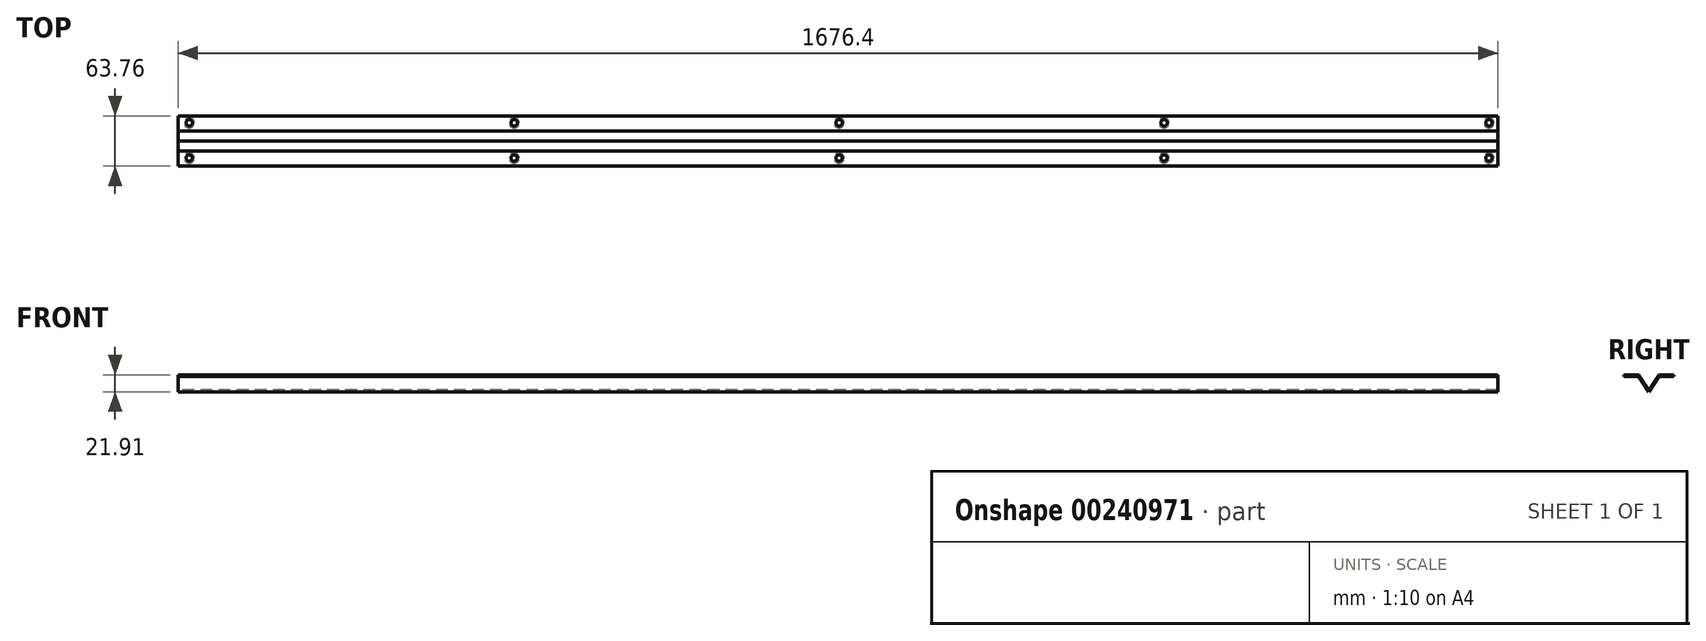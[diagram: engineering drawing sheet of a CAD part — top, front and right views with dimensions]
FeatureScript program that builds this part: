
annotation { "Feature Type Name" : "Feature", "Feature Type Description" : "" }
export const myFeature = defineFeature(function(context is Context, id is Id, definition is map)
    precondition{}
    {
        {
            var Q0;
            Q0=qCreatedBy(makeId("Right.planeOp"),FACE);
            var sketch = newSketch(context, id + "F0", { "sketchPlane" : qUnion([Q0])});
            skLineSegment(sketch, "E0", {"start": v(0, 0) * mm, "end": v(0, 19.61) * mm, "construction": true});
            skLineSegment(sketch, "E1", {"start": v(0, 19.61) * mm, "end": v(80.64, 19.61) * mm, "construction": true});
            skLineSegment(sketch, "E2", {"start": v(0, 19.61) * mm, "end": v(-83.33, 19.61) * mm, "construction": true});
            skLineSegment(sketch, "E3", {"start": v(0, 0) * mm, "end": v(12.83, 19.61) * mm});
            skLineSegment(sketch, "E4", {"start": v(12.83, 19.61) * mm, "end": v(31.88, 19.61) * mm});
            skLineSegment(sketch, "E5", {"start": v(31.88, 19.61) * mm, "end": v(31.88, 21.91) * mm});
            skLineSegment(sketch, "E6", {"start": v(31.88, 21.91) * mm, "end": v(12.83, 21.91) * mm});
            skLineSegment(sketch, "E7", {"start": v(12.83, 21.91) * mm, "end": v(0, 2.3) * mm});
            skLineSegment(sketch, "E8.MirrorCS", {"start": v(-12.83, 21.91) * mm, "end": v(0, 2.3) * mm});
            skLineSegment(sketch, "E9.MirrorCS", {"start": v(0, 0) * mm, "end": v(-12.83, 19.61) * mm});
            skLineSegment(sketch, "E10.MirrorCS", {"start": v(-12.83, 19.61) * mm, "end": v(-31.88, 19.61) * mm});
            skLineSegment(sketch, "E11.MirrorCS", {"start": v(-31.88, 21.91) * mm, "end": v(-12.83, 21.91) * mm});
            skLineSegment(sketch, "E12.MirrorCS", {"start": v(-31.88, 19.61) * mm, "end": v(-31.88, 21.91) * mm});
            skLineSegment(sketch, "E13", {"start": v(-12.83, 21.91) * mm, "end": v(-12.83, 19.61) * mm});
            skLineSegment(sketch, "E14", {"start": v(12.83, 21.91) * mm, "end": v(12.83, 19.61) * mm});
            skLineSegment(sketch, "E15", {"start": v(0, 2.3) * mm, "end": v(0, 0) * mm});
            skSolve(sketch);
        }
        {
            var Q0;
            Q0=makeQuery(id+"F0.imprint","IMPRINT",FACE,{"disambiguationData":[TD([[makeQuery(id+"F0.imprint","IMPRINT",EDGE,{"derivedFrom":sQuery(id+"F0.wireOp",EDGE,"E4")}),1.0]])]});
            var Q1;
            Q1=makeQuery(id+"F0.imprint","IMPRINT",FACE,{"disambiguationData":[TD([[makeQuery(id+"F0.imprint","IMPRINT",EDGE,{"derivedFrom":sQuery(id+"F0.wireOp",EDGE,"E3")}),1.0]])]});
            var Q2;
            Q2=makeQuery(id+"F0.imprint","IMPRINT",FACE,{"disambiguationData":[TD([[makeQuery(id+"F0.imprint","IMPRINT",EDGE,{"derivedFrom":sQuery(id+"F0.wireOp",EDGE,"E8.MirrorCS")}),-1.0]])]});
            var Q3;
            Q3=makeQuery(id+"F0.imprint","IMPRINT",FACE,{"disambiguationData":[TD([[makeQuery(id+"F0.imprint","IMPRINT",EDGE,{"derivedFrom":sQuery(id+"F0.wireOp",EDGE,"E10.MirrorCS")}),-1.0]])]});
            extrude(context, id + "F1", {"entities" : qUnion([Q0, Q1, Q2, Q3]), "depth" : 1676.4 * mm});
        }
        {
            var Q0;
            Q0=makeQuery(id+"F1.opExtrude","SWEPT_FACE",FACE,{"disambiguationData":[OSD([sQuery(id+"F0.wireOp",EDGE,"E10.MirrorCS")])]});
            var sketch = newSketch(context, id + "F2", { "sketchPlane" : qUnion([Q0])});
            skCircle(sketch, "E16", {"center": v(14.07, 21.57) * mm, "radius": 6.35 * mm});
            skCircle(sketch, "E17.0.1.0", {"center": v(14.07, -23.13) * mm, "radius": 6.35 * mm});
            skCircle(sketch, "E17.1.0.0", {"center": v(426.82, 21.57) * mm, "radius": 6.35 * mm});
            skCircle(sketch, "E17.1.1.0", {"center": v(426.82, -23.13) * mm, "radius": 6.35 * mm});
            skCircle(sketch, "E17.2.0.0", {"center": v(839.57, 21.57) * mm, "radius": 6.35 * mm});
            skCircle(sketch, "E17.2.1.0", {"center": v(839.57, -23.13) * mm, "radius": 6.35 * mm});
            skCircle(sketch, "E17.3.0.0", {"center": v(1252.32, 21.57) * mm, "radius": 6.35 * mm});
            skCircle(sketch, "E17.3.1.0", {"center": v(1252.32, -23.13) * mm, "radius": 6.35 * mm});
            skCircle(sketch, "E17.4.0.0", {"center": v(1665.07, 21.57) * mm, "radius": 6.35 * mm});
            skCircle(sketch, "E17.4.1.0", {"center": v(1665.07, -23.13) * mm, "radius": 6.35 * mm});
            skLineSegment(sketch, "E17.direction1", {"start": v(14.07, 21.57) * mm, "end": v(426.82, 21.57) * mm, "construction": true});
            skLineSegment(sketch, "E17.direction2", {"start": v(14.07, 21.57) * mm, "end": v(14.07, -23.13) * mm, "construction": true});
            skSolve(sketch);
        }
        {
            var Q0;
            Q0=sQuery(id+"F2.wireOp",VERTEX,"E16.center");
            var Q1;
            Q1=sQuery(id+"F2.wireOp",VERTEX,"E17.0.1.0.center");
            var Q2;
            Q2=sQuery(id+"F2.wireOp",VERTEX,"E17.1.1.0.center");
            var Q3;
            Q3=sQuery(id+"F2.wireOp",VERTEX,"E17.1.0.0.center");
            var Q4;
            Q4=sQuery(id+"F2.wireOp",VERTEX,"E17.2.1.0.center");
            var Q5;
            Q5=sQuery(id+"F2.wireOp",VERTEX,"E17.2.0.0.center");
            var Q6;
            Q6=sQuery(id+"F2.wireOp",VERTEX,"E17.3.1.0.center");
            var Q7;
            Q7=sQuery(id+"F2.wireOp",VERTEX,"E17.3.0.0.center");
            var Q8;
            Q8=sQuery(id+"F2.wireOp",VERTEX,"E17.4.1.0.center");
            var Q9;
            Q9=sQuery(id+"F2.wireOp",VERTEX,"E17.4.0.0.center");
            var Q10;
            Q10=makeQuery(id+"F1.opExtrude","SWEPT_BODY",BODY,{"disambiguationData":[OSD([sQuery(id+"F0.wireOp",EDGE,"E3"),sQuery(id+"F0.wireOp",EDGE,"E4"),sQuery(id+"F0.wireOp",EDGE,"E5"),sQuery(id+"F0.wireOp",EDGE,"E6"),sQuery(id+"F0.wireOp",EDGE,"E7"),sQuery(id+"F0.wireOp",EDGE,"E8.MirrorCS"),sQuery(id+"F0.wireOp",EDGE,"E9.MirrorCS"),sQuery(id+"F0.wireOp",EDGE,"E10.MirrorCS"),sQuery(id+"F0.wireOp",EDGE,"E11.MirrorCS"),sQuery(id+"F0.wireOp",EDGE,"E12.MirrorCS")])]});
            hole(context, id + "F3", {"style" : HoleStyle.C_SINK, "endStyle" : HoleEndStyle.THROUGH, "holeDiameter" : 6.35 * mm, "cSinkDiameter" : 12.7 * mm, "cSinkAngle" : 90 * degree, "tappedDepth" : 12.7 * mm, "tapClearance" : 3, "locations" : qUnion([Q0, Q1, Q2, Q3, Q4, Q5, Q6, Q7, Q8, Q9]), "scope" : qUnion([Q10])});
        }
    });
